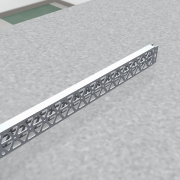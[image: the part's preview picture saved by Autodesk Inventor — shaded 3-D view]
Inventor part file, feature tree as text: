
AUTODESK INVENTOR PART (.ipt)
format: ipt  version: 2012 (Build 160160000, 160)  size: 884,736 bytes
history: native  units: in
note: dims shown in document units (in); Inventor stores cm internally (conversion verified against a paired STEP export)
features: extrude x2, fillet x2, sketch x2
ambient origin geometry x8: Origin, YZ Plane, XZ Plane, XY Plane, X Axis, Y Axis, Z Axis, Center Point
bodies: Solid1 (feature_tree)
feature tree (6):
  extrude  "Extrusion1"  Depth=3.0in
  extrude  "Extrusion2"  Depth=0.125in
  fillet  "Fillet1"  Radius=0.125in
  fillet  "Fillet2"  Radius=0.125in
  sketch  "Sketch1"  dims[d0=1.0in d1=3.0in]
  sketch  "Sketch2"  dims[d2=0.125in d3=0.125in d4=0.125in d5=0.125in d6=26.75in d7=0.0in d8=0.875in d9=0.875in d10=0.125in d11=0.125in d12=0.125in d13=0.125in d17=1.7857in d18=0.25in d19=0.125in d20=0.125in d21=0.125in d22=0.125in d23=0.25in d24=0.125in d25=0.125in d26=0.125in d27=0.125in d28=0.125in d29=0.125in d30=0.125in d31=0.25in d32=0.125in d34=0.125in d35=0.125in d36=0.25in d37=5.1181in d39=1.7857in d40=0.3937in d42=1.0in d44=0.7874in d46=1.7857in d47=0.3937in d49=1.0in d52=26.75in d53=0.0in d54=0.125in d55=0.25in d56=0.4375in d57=0.125in d58=0.125in d59=0.125in d60=0.125in d61=0.125in d62=0.125in d63=0.125in d64=0.25in d65=5.1181in d67=1.7857in d68=0.3937in d70=1.0in]
